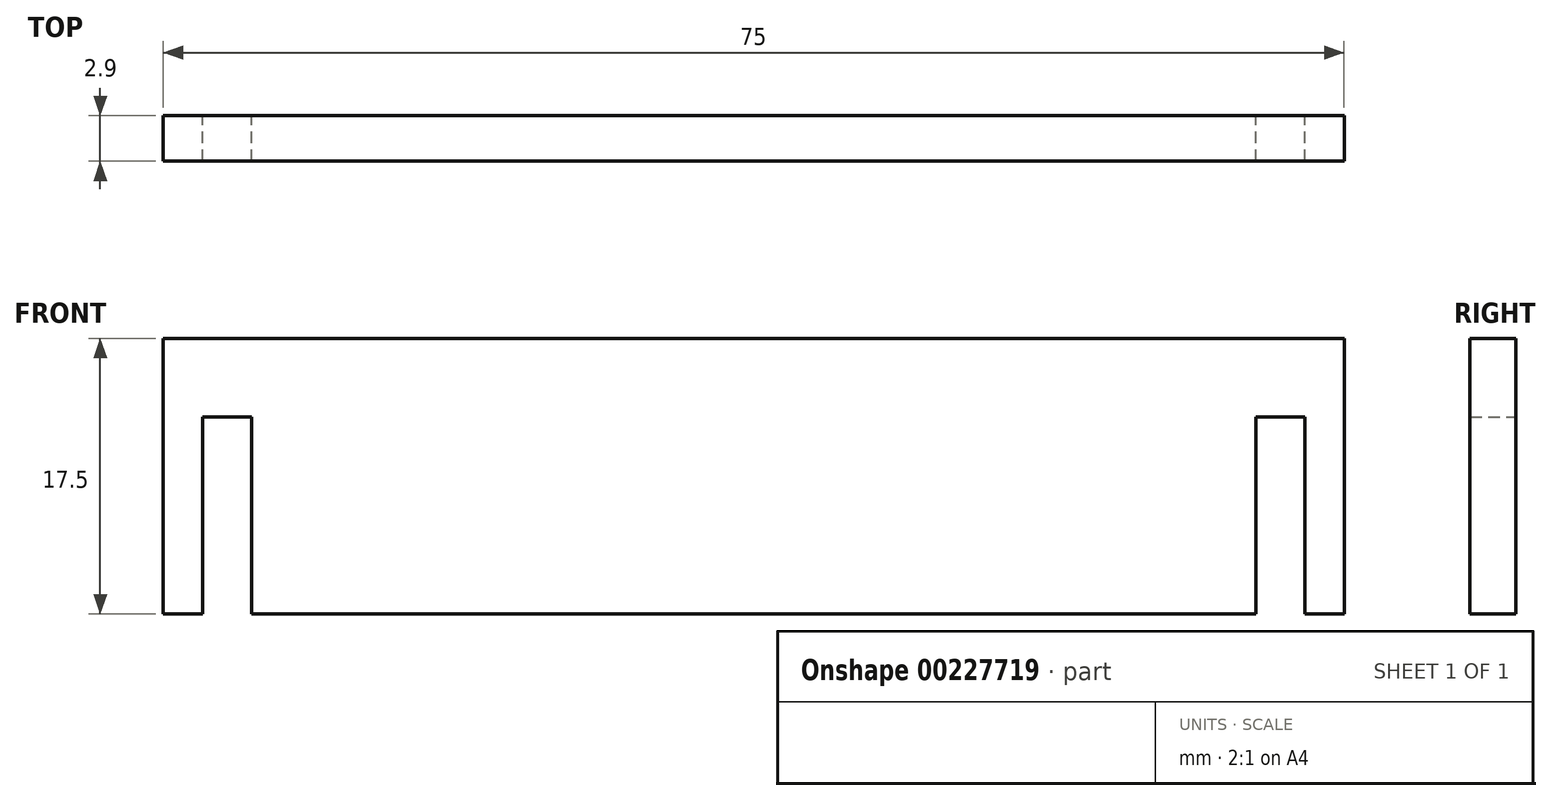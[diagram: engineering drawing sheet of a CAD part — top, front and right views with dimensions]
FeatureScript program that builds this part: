
annotation { "Feature Type Name" : "Feature", "Feature Type Description" : "" }
export const myFeature = defineFeature(function(context is Context, id is Id, definition is map)
    precondition{}
    {
        {
            var Q0;
            Q0=qCreatedBy(makeId("Front.planeOp"),FACE);
            var sketch = newSketch(context, id + "F0", { "sketchPlane" : qUnion([Q0])});
            skLineSegment(sketch, "E0.bottom", {"start": v(-32.53, 5) * mm, "end": v(42.47, 5) * mm});
            skLineSegment(sketch, "E0.top", {"start": v(-32.53, -12.5) * mm, "end": v(42.47, -12.5) * mm});
            skLineSegment(sketch, "E0.left", {"start": v(-32.53, 5) * mm, "end": v(-32.53, -12.5) * mm});
            skLineSegment(sketch, "E0.right", {"start": v(42.47, 5) * mm, "end": v(42.47, -12.5) * mm});
            skLineSegment(sketch, "E1.bottom", {"start": v(-30.03, -12.5) * mm, "end": v(-26.93, -12.5) * mm});
            skLineSegment(sketch, "E1.top", {"start": v(-30.03, 0) * mm, "end": v(-26.93, 0) * mm});
            skLineSegment(sketch, "E1.left", {"start": v(-30.03, -12.5) * mm, "end": v(-30.03, 0) * mm});
            skLineSegment(sketch, "E1.right", {"start": v(-26.93, -12.5) * mm, "end": v(-26.93, 0) * mm});
            skLineSegment(sketch, "E2.bottom", {"start": v(36.87, -12.5) * mm, "end": v(39.97, -12.5) * mm});
            skLineSegment(sketch, "E2.top", {"start": v(36.87, 0) * mm, "end": v(39.97, 0) * mm});
            skLineSegment(sketch, "E2.left", {"start": v(36.87, -12.5) * mm, "end": v(36.87, 0) * mm});
            skLineSegment(sketch, "E2.right", {"start": v(39.97, -12.5) * mm, "end": v(39.97, 0) * mm});
            skSolve(sketch);
        }
        {
            var Q0;
            Q0=makeQuery(id+"F0.imprint","IMPRINT",FACE,{"disambiguationData":[TD([[makeQuery(id+"F0.imprint","IMPRINT",EDGE,{"derivedFrom":sQuery(id+"F0.wireOp",EDGE,"E0.bottom")}),-1.0]])]});
            extrude(context, id + "F1", {"entities" : qUnion([Q0]), "depth" : 2.9 * mm});
        }
    });
